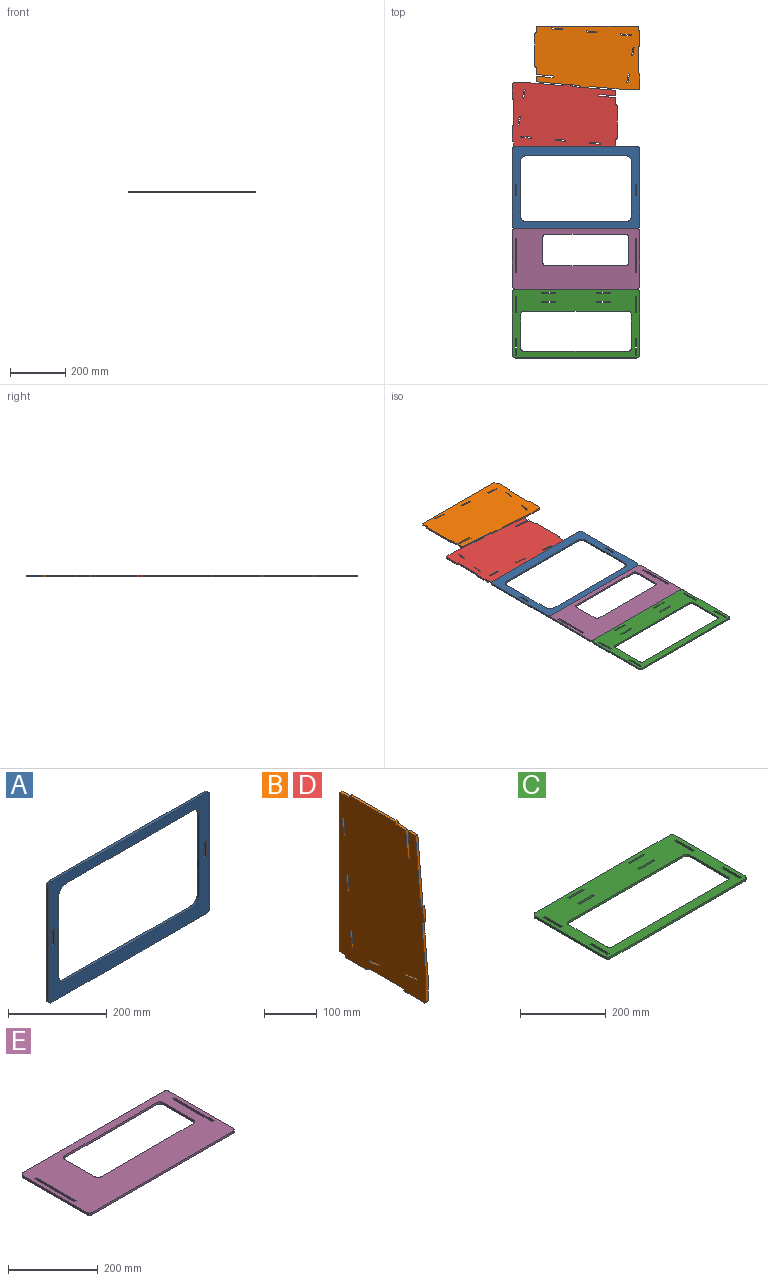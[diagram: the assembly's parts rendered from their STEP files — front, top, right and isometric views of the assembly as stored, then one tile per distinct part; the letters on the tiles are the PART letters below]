
ASSEMBLY  parts=5 mates=4
PART A: 26 faces, bbox 462x6x300 mm
  f0: plane 462x300mm, normal (0,-1,0), area 41857.5mm2, adj f2,f3,f4,f5,f6,f7,f8,f9
  f1: plane 462x300mm, normal (0,1,0), area 41857.5mm2, adj f2,f3,f4,f5,f6,f7,f8,f9
  f2: plane 442x6mm, normal (0,0,1), area 2652mm2, adj f0,f1,f6,f9
  f3: plane 280x6mm, normal (-1,0,0), area 1680mm2, adj f0,f1,f6,f7
  f4: plane 442x6mm, normal (0,0,-1), area 2652mm2, adj f0,f1,f7,f8
  f5: plane 280x6mm, normal (1,0,0), area 1680mm2, adj f0,f1,f8,f9
  f6: cylinder r=10mm len=10mm, axis (0,-1,0), area 94.2mm2, adj f0,f1,f2,f3
  f7: cylinder r=10mm len=10mm, axis (0,1,0), area 94.2mm2, adj f0,f1,f3,f4
  f8: cylinder r=10mm len=10mm, axis (0,-1,0), area 94.2mm2, adj f0,f1,f4,f5
  f9: cylinder r=10mm len=10mm, axis (0,1,0), area 94.2mm2, adj f0,f1,f2,f5
  f10: plane 200x6mm, normal (-1,0,0), area 1200mm2, adj f0,f1,f11,f17
  f11: cylinder r=20mm len=20mm, axis (0,1,0), area 188.5mm2, adj f0,f1,f10,f12
  f12: plane 362x6mm, normal (0,0,-1), area 2172mm2, adj f0,f1,f11,f13
  f13: cylinder r=20mm len=20mm, axis (0,1,0), area 188.5mm2, adj f0,f1,f12,f14
  f14: plane 200x6mm, normal (1,0,0), area 1200mm2, adj f0,f1,f13,f15
  f15: cylinder r=20mm len=20mm, axis (0,1,0), area 188.5mm2, adj f0,f1,f14,f16
  f16: plane 362x6mm, normal (0,0,1), area 2172mm2, adj f0,f1,f15,f17
  f17: cylinder r=20mm len=20mm, axis (0,1,0), area 188.5mm2, adj f0,f1,f10,f16
  f18: plane 40x6mm, normal (1,0,0), area 240mm2, adj f0,f1,f19,f20
  f19: plane 6.5x6mm, normal (0,0,1), area 39mm2, adj f0,f1,f18,f21
  f20: plane 6.5x6mm, normal (0,0,-1), area 39mm2, adj f0,f1,f18,f21
  f21: plane 40x6mm, normal (-1,0,0), area 240mm2, adj f0,f1,f19,f20
  f22: plane 6.5x6mm, normal (0,0,1), area 39mm2, adj f0,f1,f23,f25
  f23: plane 40x6mm, normal (-1,0,0), area 240mm2, adj f0,f1,f22,f24
  f24: plane 6.5x6mm, normal (0,0,-1), area 39mm2, adj f0,f1,f23,f25
  f25: plane 40x6mm, normal (1,0,0), area 240mm2, adj f0,f1,f22,f24
PART B: 52 faces, bbox 6x230x380 mm
  f0: plane 155.61x13.61mm, normal (0,-1,0.09), area 937.2mm2, adj f4,f5,f6,f49
  f1: plane 95x6mm, normal (0,0,-1), area 570mm2, adj f5,f6,f38,f42
  f2: plane 15x6mm, normal (0,0,-1), area 90mm2, adj f5,f6,f9,f37
  f3: plane 26.14x6mm, normal (0,0,1), area 156.8mm2, adj f5,f6,f23,f35
  f4: plane 20.08x6mm, normal (0,0,1), area 120.5mm2, adj f0,f5,f6,f25
  f5: plane 380x230mm, normal (1,0,0), area 80987.9mm2, adj f0,f1,f2,f3,f4,f7,f8,f9
  f6: plane 380x230mm, normal (-1,0,0), area 80987.9mm2, adj f0,f1,f2,f3,f4,f7,f8,f9
  f7: plane 121.54x10.63mm, normal (0,-1,0.09), area 732mm2, adj f5,f6,f8,f51
  f8: plane 55x6mm, normal (0,-1,0), area 330mm2, adj f5,f6,f7,f40
  f9: plane 370x6mm, normal (0,1,0), area 2220mm2, adj f2,f5,f6,f10
  f10: plane 25x6mm, normal (0,0,1), area 150mm2, adj f5,f6,f9,f34
  f11: plane 6x4.18mm, normal (0,0.09,1), area 25.2mm2, adj f5,f6,f12,f14
  f12: plane 39.85x6mm, normal (0,-1,0.09), area 240mm2, adj f5,f6,f11,f13
  f13: plane 6x4.18mm, normal (0,-0.09,-1), area 25.2mm2, adj f5,f6,f12,f14
  f14: plane 39.85x6mm, normal (0,1,-0.09), area 240mm2, adj f5,f6,f11,f13
  f15: plane 6x4.18mm, normal (0,0.09,1), area 25.2mm2, adj f5,f6,f16,f18
  f16: plane 39.85x6mm, normal (0,-1,0.09), area 240mm2, adj f5,f6,f15,f17
  f17: plane 6x4.18mm, normal (0,-0.09,-1), area 25.2mm2, adj f5,f6,f16,f18
  f18: plane 39.85x6mm, normal (0,1,-0.09), area 240mm2, adj f5,f6,f15,f17
  f19: plane 6x4.18mm, normal (0,-0.09,-1), area 25.2mm2, adj f5,f6,f20,f21
  f20: plane 39.85x6mm, normal (0,1,-0.09), area 240mm2, adj f5,f6,f19,f22
  f21: plane 39.85x6mm, normal (0,-1,0.09), area 240mm2, adj f5,f6,f19,f22
  f22: plane 6x4.18mm, normal (0,0.09,1), area 25.2mm2, adj f5,f6,f20,f21
  f23: plane 61.31x6mm, normal (0,-1,0.09), area 369.3mm2, adj f3,f5,f6,f24
  f24: plane 6.18x6mm, normal (0,0.09,1), area 37.2mm2, adj f5,f6,f23,f25
  f25: plane 60.77x6mm, normal (0,1,-0.09), area 366mm2, adj f4,f5,f6,f24
  f26: plane 6x4.04mm, normal (0,-0.98,0.17), area 24.6mm2, adj f5,f6,f27,f28
  f27: plane 31.51x6mm, normal (0,-0.17,-0.98), area 192mm2, adj f5,f6,f26,f29
  f28: plane 31.51x6mm, normal (0,0.17,0.98), area 192mm2, adj f5,f6,f26,f29
  f29: plane 6x4.04mm, normal (0,0.98,-0.17), area 24.6mm2, adj f5,f6,f27,f28
  f30: plane 6x4.04mm, normal (0,-0.98,0.17), area 24.6mm2, adj f5,f6,f31,f32
  f31: plane 29.74x6mm, normal (0,-0.17,-0.98), area 181.2mm2, adj f5,f6,f30,f33
  f32: plane 29.74x6mm, normal (0,0.17,0.98), area 181.2mm2, adj f5,f6,f30,f33
  f33: plane 6x4.04mm, normal (0,0.98,-0.17), area 24.6mm2, adj f5,f6,f31,f32
  f34: plane 6x2.26mm, normal (0,1,0.09), area 13.6mm2, adj f5,f6,f10,f47
  f35: plane 6x2.26mm, normal (0,-1,0.09), area 13.6mm2, adj f3,f5,f6,f48
  f36: plane 118.63x6mm, normal (0,0,1), area 711.8mm2, adj f5,f6,f47,f48
  f37: plane 6x2.26mm, normal (0,1,-0.09), area 13.6mm2, adj f2,f5,f6,f46
  f38: plane 6x2.26mm, normal (0,-1,-0.09), area 13.6mm2, adj f1,f5,f6,f45
  f39: plane 53.63x6mm, normal (0,0,-1), area 321.8mm2, adj f5,f6,f45,f46
  f40: plane 6x2.72mm, normal (0,-0.95,-0.32), area 17.2mm2, adj f5,f6,f8,f43
  f41: plane 52.46x6mm, normal (0,0,-1), area 314.8mm2, adj f5,f6,f43,f44
  f42: plane 6x2.72mm, normal (0,0.95,-0.32), area 17.2mm2, adj f1,f5,f6,f44
  f43: cylinder r=3mm len=6mm, axis (-1,0,0), area 22.3mm2, adj f5,f6,f40,f41
  f44: cylinder r=3mm len=6mm, axis (-1,0,0), area 22.3mm2, adj f5,f6,f41,f42
  f45: cylinder r=3mm len=6mm, axis (-1,0,0), area 26.7mm2, adj f5,f6,f38,f39
  f46: cylinder r=3mm len=6mm, axis (-1,0,0), area 26.7mm2, adj f5,f6,f37,f39
  f47: cylinder r=3mm len=6mm, axis (-1,0,0), area 26.7mm2, adj f5,f6,f34,f36
  f48: cylinder r=3mm len=6mm, axis (-1,0,0), area 26.7mm2, adj f5,f6,f35,f36
  f49: plane 6x4.98mm, normal (0,0.09,1), area 30mm2, adj f0,f5,f6,f50
  f50: plane 29.23x6mm, normal (0,-1,0.09), area 176mm2, adj f5,f6,f49,f51
  f51: cylinder r=10mm len=9.06mm, axis (1,0,0), area 62.8mm2, adj f5,f6,f7,f50
PART C: 50 faces, bbox 462x250x6 mm
  f0: plane 462x250mm, normal (0,0,1), area 55060mm2, adj f2,f3,f4,f5,f6,f7,f8,f9
  f1: plane 462x250mm, normal (0,0,-1), area 55060mm2, adj f2,f3,f4,f5,f6,f7,f8,f9
  f2: plane 442x6mm, normal (0,1,0), area 2652mm2, adj f0,f1,f38,f41
  f3: plane 230x6mm, normal (-1,0,0), area 1380mm2, adj f0,f1,f38,f39
  f4: plane 442x6mm, normal (0,-1,0), area 2652mm2, adj f0,f1,f39,f40
  f5: plane 230x6mm, normal (1,0,0), area 1380mm2, adj f0,f1,f40,f41
  f6: plane 60x6mm, normal (-1,0,0), area 360mm2, adj f0,f1,f7,f9
  f7: plane 6x6mm, normal (0,-1,0), area 36mm2, adj f0,f1,f6,f8
  f8: plane 60x6mm, normal (1,0,0), area 360mm2, adj f0,f1,f7,f9
  f9: plane 6x6mm, normal (0,1,0), area 36mm2, adj f0,f1,f6,f8
  f10: plane 6x6mm, normal (0,-1,0), area 36mm2, adj f0,f1,f11,f12
  f11: plane 60x6mm, normal (-1,0,0), area 360mm2, adj f0,f1,f10,f13
  f12: plane 60x6mm, normal (1,0,0), area 360mm2, adj f0,f1,f10,f13
  f13: plane 6x6mm, normal (0,1,0), area 36mm2, adj f0,f1,f11,f12
  f14: plane 60x6mm, normal (1,0,0), area 360mm2, adj f0,f1,f15,f16
  f15: plane 6x6mm, normal (0,-1,0), area 36mm2, adj f0,f1,f14,f17
  f16: plane 6x6mm, normal (0,1,0), area 36mm2, adj f0,f1,f14,f17
  f17: plane 60x6mm, normal (-1,0,0), area 360mm2, adj f0,f1,f15,f16
  f18: plane 60x6mm, normal (1,0,0), area 360mm2, adj f0,f1,f19,f20
  f19: plane 6x6mm, normal (0,-1,0), area 36mm2, adj f0,f1,f18,f21
  f20: plane 6x6mm, normal (0,1,0), area 36mm2, adj f0,f1,f18,f21
  f21: plane 60x6mm, normal (-1,0,0), area 360mm2, adj f0,f1,f19,f20
  f22: plane 50x6mm, normal (0,-1,0), area 300mm2, adj f0,f1,f23,f24
  f23: plane 6x5.5mm, normal (1,0,0), area 33mm2, adj f0,f1,f22,f25
  f24: plane 6x5.5mm, normal (-1,0,0), area 33mm2, adj f0,f1,f22,f25
  f25: plane 50x6mm, normal (0,1,0), area 300mm2, adj f0,f1,f23,f24
  f26: plane 6x5.5mm, normal (1,0,0), area 33mm2, adj f0,f1,f27,f28
  f27: plane 50x6mm, normal (0,1,0), area 300mm2, adj f0,f1,f26,f29
  f28: plane 50x6mm, normal (0,-1,0), area 300mm2, adj f0,f1,f26,f29
  f29: plane 6x5.5mm, normal (-1,0,0), area 33mm2, adj f0,f1,f27,f28
  f30: plane 6x4.5mm, normal (1,0,0), area 27mm2, adj f0,f1,f31,f32
  f31: plane 50x6mm, normal (0,-1,0), area 300mm2, adj f0,f1,f30,f33
  f32: plane 50x6mm, normal (0,1,0), area 300mm2, adj f0,f1,f30,f33
  f33: plane 6x4.5mm, normal (-1,0,0), area 27mm2, adj f0,f1,f31,f32
  f34: plane 6x4.5mm, normal (1,0,0), area 27mm2, adj f0,f1,f35,f36
  f35: plane 50x6mm, normal (0,-1,0), area 300mm2, adj f0,f1,f34,f37
  f36: plane 50x6mm, normal (0,1,0), area 300mm2, adj f0,f1,f34,f37
  f37: plane 6x4.5mm, normal (-1,0,0), area 27mm2, adj f0,f1,f35,f36
  f38: cylinder r=10mm len=10mm, axis (0,0,1), area 94.2mm2, adj f0,f1,f2,f3
  f39: cylinder r=10mm len=10mm, axis (0,0,-1), area 94.2mm2, adj f0,f1,f3,f4
  f40: cylinder r=10mm len=10mm, axis (0,0,1), area 94.2mm2, adj f0,f1,f4,f5
  f41: cylinder r=10mm len=10mm, axis (0,0,-1), area 94.2mm2, adj f0,f1,f2,f5
  f42: plane 380x6mm, normal (0,1,0), area 2280mm2, adj f0,f1,f43,f49
  f43: cylinder r=10mm len=10mm, axis (0,0,1), area 94.2mm2, adj f0,f1,f42,f44
  f44: plane 125x6mm, normal (-1,0,0), area 750mm2, adj f0,f1,f43,f45
  f45: cylinder r=10mm len=10mm, axis (0,0,1), area 94.2mm2, adj f0,f1,f44,f46
  f46: plane 380x6mm, normal (0,-1,0), area 2280mm2, adj f0,f1,f45,f47
  f47: cylinder r=10mm len=10mm, axis (0,0,1), area 94.2mm2, adj f0,f1,f46,f48
  f48: plane 125x6mm, normal (1,0,0), area 750mm2, adj f0,f1,f47,f49
  f49: cylinder r=10mm len=10mm, axis (0,0,1), area 94.2mm2, adj f0,f1,f42,f48
PART D: same geometry as B
PART E: 26 faces, bbox 462x219x6 mm
  f0: plane 462x219mm, normal (0,0,1), area 63971.8mm2, adj f2,f3,f4,f5,f6,f7,f8,f9
  f1: plane 462x219mm, normal (0,0,-1), area 63971.8mm2, adj f2,f3,f4,f5,f6,f7,f8,f9
  f2: plane 442x6mm, normal (0,1,0), area 2652mm2, adj f0,f1,f14,f17
  f3: plane 199x6mm, normal (-1,0,0), area 1194mm2, adj f0,f1,f14,f15
  f4: plane 442x6mm, normal (0,-1,0), area 2652mm2, adj f0,f1,f15,f16
  f5: plane 199x6mm, normal (1,0,0), area 1194mm2, adj f0,f1,f16,f17
  f6: plane 125.5x6mm, normal (1,0,0), area 753mm2, adj f0,f1,f7,f8
  f7: plane 6.2x6mm, normal (0,-1,0), area 37.2mm2, adj f0,f1,f6,f9
  f8: plane 6.2x6mm, normal (0,1,0), area 37.2mm2, adj f0,f1,f6,f9
  f9: plane 125.5x6mm, normal (-1,0,0), area 753mm2, adj f0,f1,f7,f8
  f10: plane 125.5x6mm, normal (-1,0,0), area 753mm2, adj f0,f1,f11,f13
  f11: plane 6.2x6mm, normal (0,-1,0), area 37.2mm2, adj f0,f1,f10,f12
  f12: plane 125.5x6mm, normal (1,0,0), area 753mm2, adj f0,f1,f11,f13
  f13: plane 6.2x6mm, normal (0,1,0), area 37.2mm2, adj f0,f1,f10,f12
  f14: cylinder r=10mm len=10mm, axis (0,0,1), area 94.2mm2, adj f0,f1,f2,f3
  f15: cylinder r=10mm len=10mm, axis (0,0,-1), area 94.2mm2, adj f0,f1,f3,f4
  f16: cylinder r=10mm len=10mm, axis (0,0,1), area 94.2mm2, adj f0,f1,f4,f5
  f17: cylinder r=10mm len=10mm, axis (0,0,-1), area 94.2mm2, adj f0,f1,f2,f5
  f18: plane 290x6mm, normal (0,-1,0), area 1740mm2, adj f0,f1,f22,f23
  f19: plane 95x6mm, normal (-1,0,0), area 570mm2, adj f0,f1,f22,f24
  f20: plane 95x6mm, normal (1,0,0), area 570mm2, adj f0,f1,f23,f25
  f21: plane 290x6mm, normal (0,1,0), area 1740mm2, adj f0,f1,f24,f25
  f22: cylinder r=10mm len=10mm, axis (0,0,1), area 94.2mm2, adj f0,f1,f18,f19
  f23: cylinder r=10mm len=10mm, axis (0,0,-1), area 94.2mm2, adj f0,f1,f18,f20
  f24: cylinder r=10mm len=10mm, axis (0,0,-1), area 94.2mm2, adj f0,f1,f19,f21
  f25: cylinder r=10mm len=10mm, axis (0,0,1), area 94.2mm2, adj f0,f1,f20,f21
PLACE A rot(axis=(1,0,0),90deg) t=(231,769,0)mm
PLACE B rot(axis=(0,-1,0),90deg) t=(457,975,-6)mm
PLACE C t=(231,250,-6)mm
PLACE D rot(axis=(0.71,0,0.71),180deg) t=(5,999,-6)mm
PLACE E t=(231,469,-6)mm
MATE fastened E.f0 <-> A.f1  axis (0,0,1) through (10,469,0)mm
MATE fastened A.f1 <-> B.f5  axis (0,0,1) through (452,769,0)mm
MATE fastened E.f0 <-> C.f0  axis (0,0,1) through (10,250,0)mm
MATE fastened D.f5 <-> A.f1  axis (0,0,1) through (5,769,0)mm
